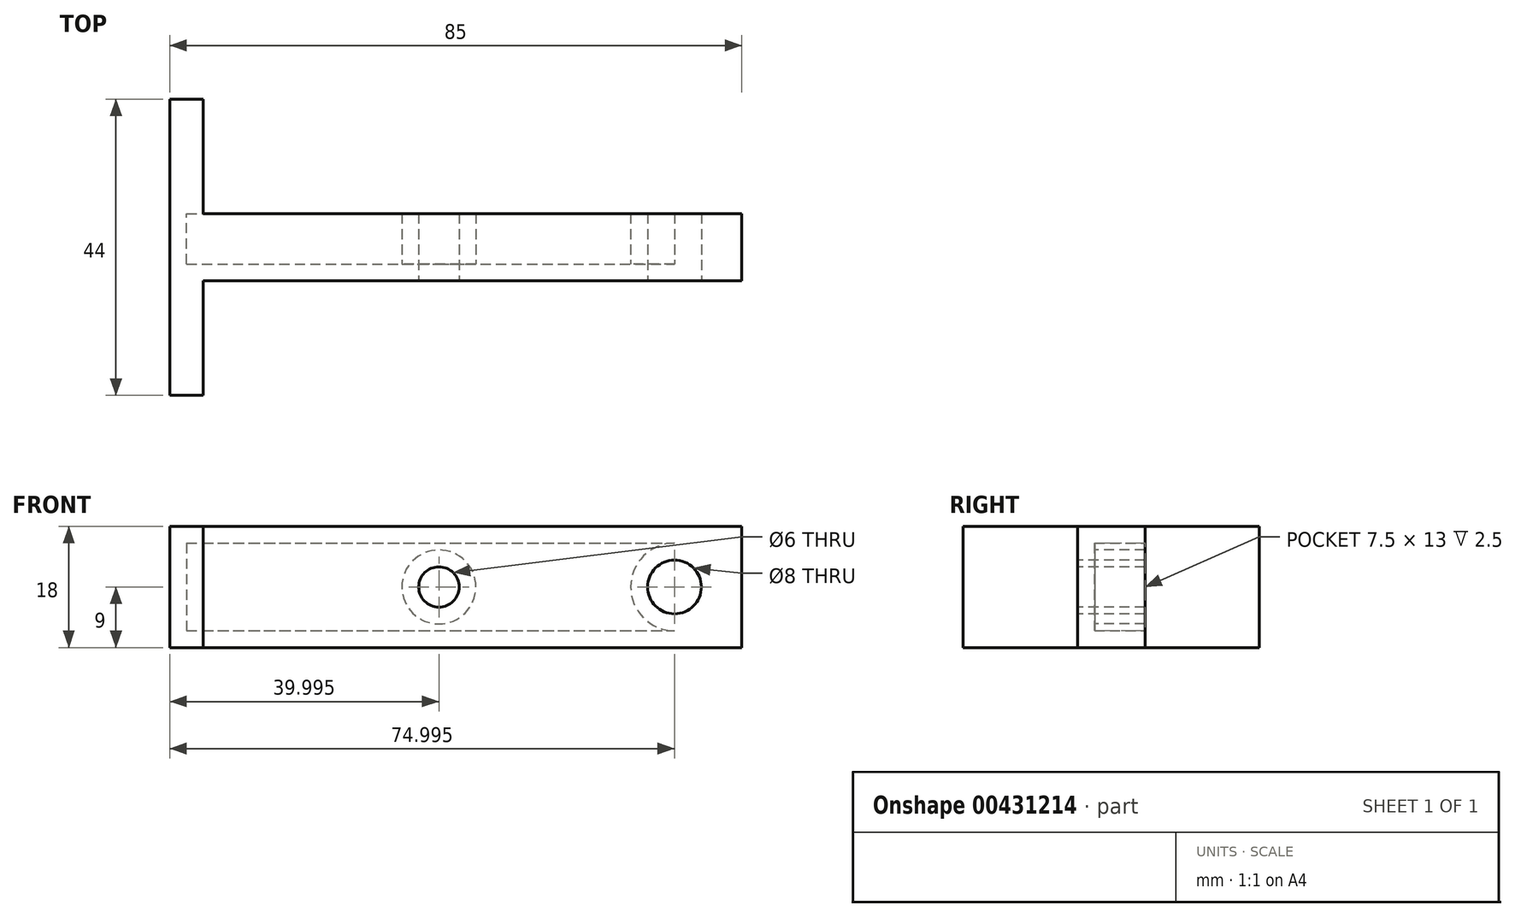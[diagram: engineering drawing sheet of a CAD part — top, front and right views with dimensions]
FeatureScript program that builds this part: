
annotation { "Feature Type Name" : "Feature", "Feature Type Description" : "" }
export const myFeature = defineFeature(function(context is Context, id is Id, definition is map)
    precondition{}
    {
        {
            var Q0;
            Q0=qCreatedBy(makeId("Top.planeOp"),FACE);
            var sketch = newSketch(context, id + "F0", { "sketchPlane" : qUnion([Q0])});
            skLineSegment(sketch, "E0.bottom", {"start": v(-56.61, -0.7) * mm, "end": v(23.39, -0.7) * mm});
            skLineSegment(sketch, "E0.top", {"start": v(-56.61, -10.7) * mm, "end": v(23.39, -10.7) * mm});
            skLineSegment(sketch, "E0.right", {"start": v(23.39, -0.7) * mm, "end": v(23.39, -10.7) * mm});
            skLineSegment(sketch, "E1.bottom", {"start": v(-61.61, -27.7) * mm, "end": v(-56.61, -27.7) * mm});
            skLineSegment(sketch, "E1.top", {"start": v(-61.61, 16.3) * mm, "end": v(-56.61, 16.3) * mm});
            skLineSegment(sketch, "E1.left", {"start": v(-61.61, -27.7) * mm, "end": v(-61.61, 16.3) * mm});
            skLineSegment(sketch, "E1.right", {"start": v(-56.61, -27.7) * mm, "end": v(-56.61, -10.7) * mm});
            skLineSegment(sketch, "E2.trimOffspring", {"start": v(-56.61, -0.7) * mm, "end": v(-56.61, 16.3) * mm});
            skSolve(sketch);
        }
        {
            var Q0;
            Q0 = qSketchRegion(id + "F0", true);
            extrude(context, id + "F1", {"entities" : qUnion([Q0]), "depth" : 18 * mm});
        }
        {
            var Q0;
            Q0=makeQuery(id+"F1.opExtrude","SWEPT_FACE",FACE,{"disambiguationData":[OSD([sQuery(id+"F0.wireOp",EDGE,"E0.top")])]});
            var sketch = newSketch(context, id + "F2", { "sketchPlane" : qUnion([Q0])});
            skPoint(sketch, "E3", {"position": v(-21.61, 9) * mm});
            skPoint(sketch, "E4", {"position": v(13.39, 9) * mm});
            skSolve(sketch);
        }
        {
            var Q0;
            Q0=sQuery(id+"F2.wireOp",VERTEX,"E3");
            var Q1;
            Q1=makeQuery(id+"F1.opExtrude","SWEPT_BODY",BODY,{"disambiguationData":[OSD([sQuery(id+"F0.wireOp",EDGE,"E0.bottom"),sQuery(id+"F0.wireOp",EDGE,"E0.top"),sQuery(id+"F0.wireOp",EDGE,"E0.right"),sQuery(id+"F0.wireOp",EDGE,"E1.bottom"),sQuery(id+"F0.wireOp",EDGE,"E1.top"),sQuery(id+"F0.wireOp",EDGE,"E1.left"),sQuery(id+"F0.wireOp",EDGE,"E1.right"),sQuery(id+"F0.wireOp",EDGE,"E2.trimOffspring")])]});
            hole(context, id + "F3", {"style" : HoleStyle.SIMPLE, "endStyle" : HoleEndStyle.THROUGH, "holeDiameter" : 6 * mm, "isTappedThrough" : true, "tappedDepth" : 12 * mm, "tapClearance" : 3, "locations" : qUnion([Q0]), "scope" : qUnion([Q1])});
        }
        {
            var Q0;
            Q0=sQuery(id+"F2.wireOp",VERTEX,"E4");
            var Q1;
            Q1=makeQuery(id+"F1.opExtrude","SWEPT_BODY",BODY,{"disambiguationData":[OSD([sQuery(id+"F0.wireOp",EDGE,"E0.bottom"),sQuery(id+"F0.wireOp",EDGE,"E0.top"),sQuery(id+"F0.wireOp",EDGE,"E0.right"),sQuery(id+"F0.wireOp",EDGE,"E1.bottom"),sQuery(id+"F0.wireOp",EDGE,"E1.top"),sQuery(id+"F0.wireOp",EDGE,"E1.left"),sQuery(id+"F0.wireOp",EDGE,"E1.right"),sQuery(id+"F0.wireOp",EDGE,"E2.trimOffspring")])]});
            hole(context, id + "F4", {"style" : HoleStyle.SIMPLE, "endStyle" : HoleEndStyle.THROUGH, "holeDiameter" : 8 * mm, "isTappedThrough" : true, "tappedDepth" : 12 * mm, "tapClearance" : 3, "locations" : qUnion([Q0]), "scope" : qUnion([Q1])});
        }
        {
            var Q0;
            Q0=makeQuery(id+"F1.opExtrude","SWEPT_FACE",FACE,{"disambiguationData":[OSD([sQuery(id+"F0.wireOp",EDGE,"E0.bottom")])]});
            shell(context, id + "F5", {"entities" : qUnion([Q0]), "thickness" : 2.5 * mm});
        }
    });
